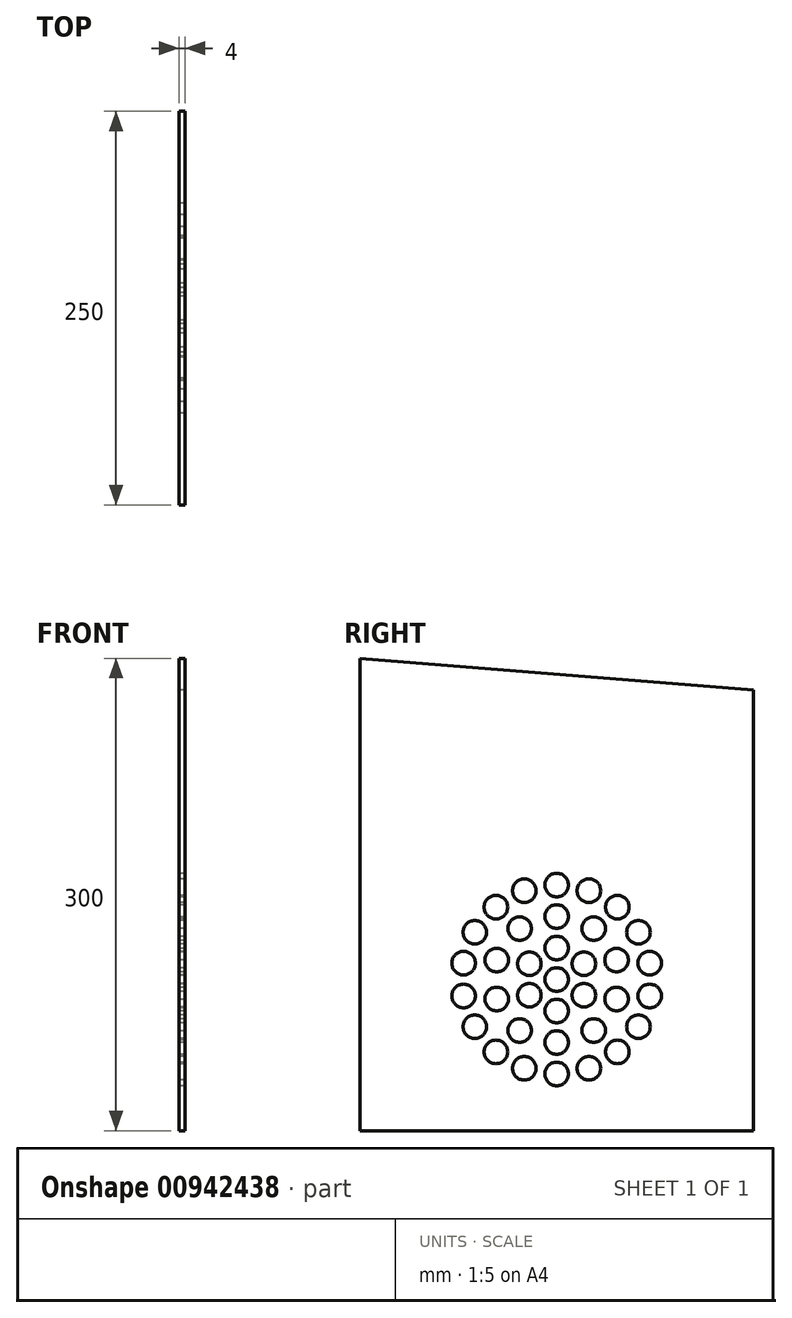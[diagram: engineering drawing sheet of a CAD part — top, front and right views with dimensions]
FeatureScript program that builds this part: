
annotation { "Feature Type Name" : "Feature", "Feature Type Description" : "" }
export const myFeature = defineFeature(function(context is Context, id is Id, definition is map)
    precondition{}
    {
        {
            var Q0;
            Q0=qCreatedBy(makeId("Right.planeOp"),FACE);
            var sketch = newSketch(context, id + "F0", { "sketchPlane" : qUnion([Q0])});
            skLineSegment(sketch, "E0.bottom", {"start": v(-125, 0) * mm, "end": v(125, 0) * mm});
            skLineSegment(sketch, "E0.left", {"start": v(-125, 0) * mm, "end": v(-125, 300) * mm});
            skLineSegment(sketch, "E0.right", {"start": v(125, 0) * mm, "end": v(125, 280) * mm});
            skLineSegment(sketch, "E1", {"start": v(-125, 300) * mm, "end": v(125, 280) * mm});
            skCircle(sketch, "E2", {"center": v(0, 96) * mm, "radius": 7.5 * mm});
            skCircle(sketch, "E3.0.1.0", {"center": v(0, 116) * mm, "radius": 7.5 * mm});
            skCircle(sketch, "E3.0.2.0", {"center": v(0, 136) * mm, "radius": 7.5 * mm});
            skCircle(sketch, "E3.0.3.0", {"center": v(0, 156) * mm, "radius": 7.5 * mm});
            skLineSegment(sketch, "E3.direction1", {"start": v(0, 96) * mm, "end": v(25, 96) * mm, "construction": true});
            skLineSegment(sketch, "E3.direction2", {"start": v(0, 96) * mm, "end": v(0, 116) * mm, "construction": true});
            skCircle(sketch, "E4.1.0", {"center": v(-17.32, 106) * mm, "radius": 7.5 * mm});
            skCircle(sketch, "E4.2.0", {"center": v(-17.32, 86) * mm, "radius": 7.5 * mm});
            skCircle(sketch, "E4.3.0", {"center": v(0, 76) * mm, "radius": 7.5 * mm});
            skCircle(sketch, "E4.4.0", {"center": v(17.32, 86) * mm, "radius": 7.5 * mm});
            skCircle(sketch, "E5.1.0", {"center": v(-23.51, 128.36) * mm, "radius": 7.5 * mm});
            skCircle(sketch, "E5.2.0", {"center": v(-38.04, 108.36) * mm, "radius": 7.5 * mm});
            skCircle(sketch, "E5.3.0", {"center": v(-38.04, 83.64) * mm, "radius": 7.5 * mm});
            skCircle(sketch, "E5.4.0", {"center": v(-23.51, 63.64) * mm, "radius": 7.5 * mm});
            skCircle(sketch, "E5.5.0", {"center": v(0, 56) * mm, "radius": 7.5 * mm});
            skCircle(sketch, "E5.6.0", {"center": v(23.51, 63.64) * mm, "radius": 7.5 * mm});
            skCircle(sketch, "E5.7.0", {"center": v(38.04, 83.64) * mm, "radius": 7.5 * mm});
            skCircle(sketch, "E5.8.0", {"center": v(38.04, 108.36) * mm, "radius": 7.5 * mm});
            skCircle(sketch, "E6.1.0", {"center": v(-20.52, 152.38) * mm, "radius": 7.5 * mm});
            skCircle(sketch, "E6.2.0", {"center": v(-38.57, 141.96) * mm, "radius": 7.5 * mm});
            skCircle(sketch, "E6.3.0", {"center": v(-51.96, 126) * mm, "radius": 7.5 * mm});
            skCircle(sketch, "E6.4.0", {"center": v(-59.09, 106.42) * mm, "radius": 7.5 * mm});
            skCircle(sketch, "E6.5.0", {"center": v(-59.09, 85.58) * mm, "radius": 7.5 * mm});
            skCircle(sketch, "E6.6.0", {"center": v(-51.96, 66) * mm, "radius": 7.5 * mm});
            skCircle(sketch, "E6.7.0", {"center": v(-38.57, 50.04) * mm, "radius": 7.5 * mm});
            skCircle(sketch, "E6.8.0", {"center": v(-20.52, 39.62) * mm, "radius": 7.5 * mm});
            skCircle(sketch, "E6.9.0", {"center": v(0, 36) * mm, "radius": 7.5 * mm});
            skCircle(sketch, "E6.10.0", {"center": v(20.52, 39.62) * mm, "radius": 7.5 * mm});
            skCircle(sketch, "E6.11.0", {"center": v(38.57, 50.04) * mm, "radius": 7.5 * mm});
            skCircle(sketch, "E6.12.0", {"center": v(51.96, 66) * mm, "radius": 7.5 * mm});
            skCircle(sketch, "E6.13.0", {"center": v(59.09, 85.58) * mm, "radius": 7.5 * mm});
            skCircle(sketch, "E6.14.0", {"center": v(59.09, 106.42) * mm, "radius": 7.5 * mm});
            skCircle(sketch, "E7.1.5.0", {"center": v(17.32, 106) * mm, "radius": 7.5 * mm});
            skCircle(sketch, "E8.1.9.0", {"center": v(23.51, 128.36) * mm, "radius": 7.5 * mm});
            skCircle(sketch, "E9.1.15.0", {"center": v(51.96, 126) * mm, "radius": 7.5 * mm});
            skCircle(sketch, "E9.1.16.0", {"center": v(38.57, 141.96) * mm, "radius": 7.5 * mm});
            skCircle(sketch, "E10.1.17.0", {"center": v(20.52, 152.38) * mm, "radius": 7.5 * mm});
            skSolve(sketch);
        }
        {
            var Q0;
            Q0 = qSketchRegion(id + "F0", true);
            extrude(context, id + "F1", {"entities" : qUnion([Q0]), "depth" : 4 * mm, "offsetDistance" : 25 * mm});
        }
    });
